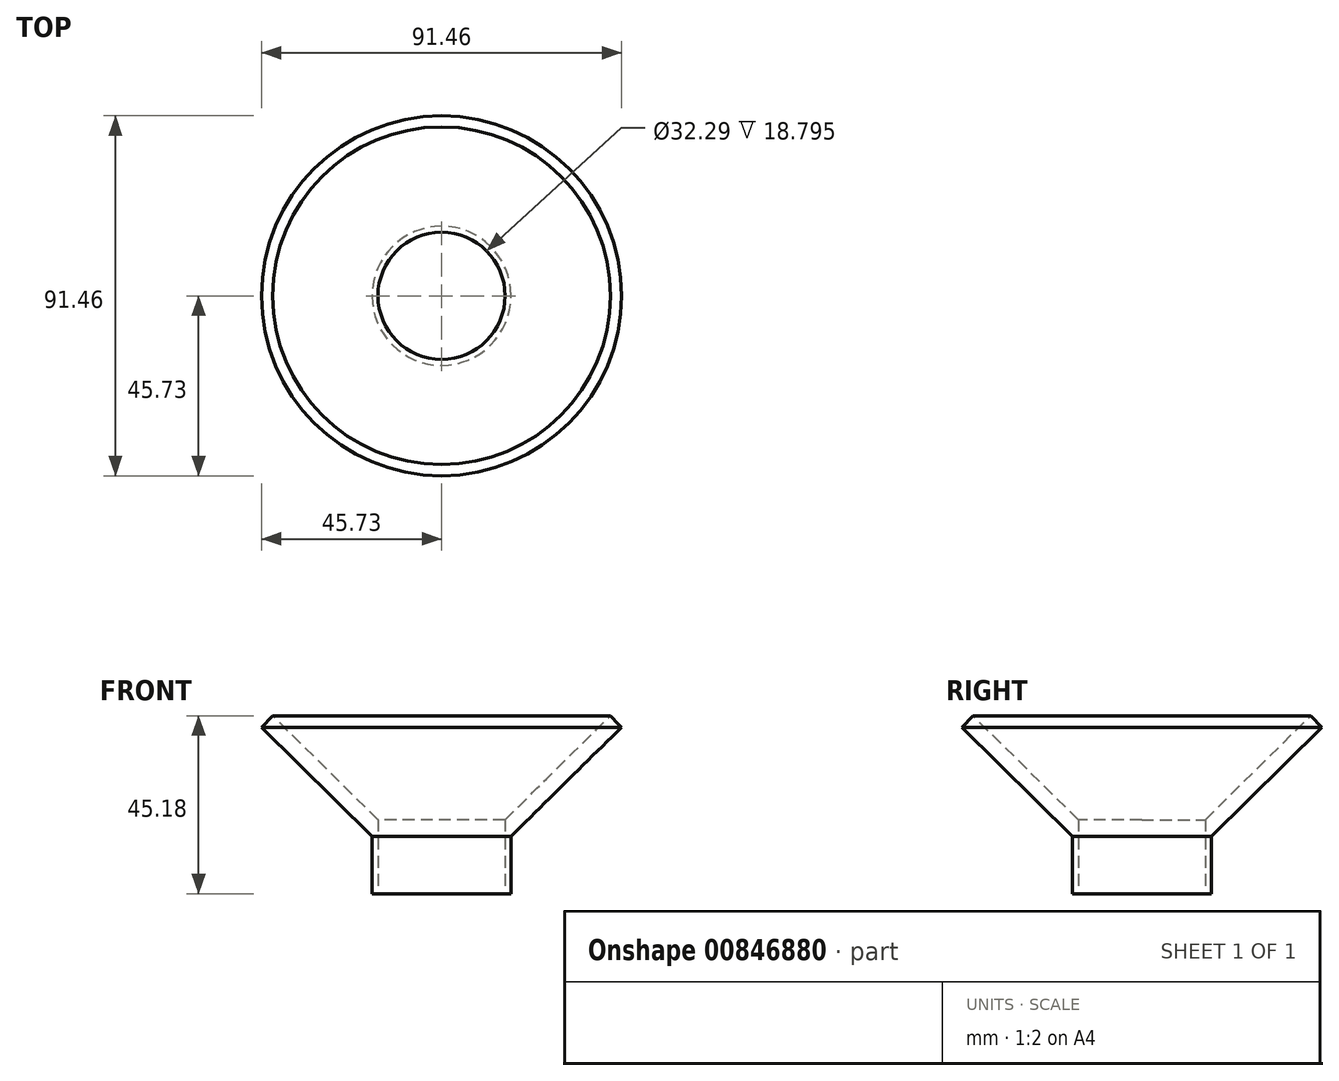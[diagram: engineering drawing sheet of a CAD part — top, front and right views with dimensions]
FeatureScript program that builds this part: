
annotation { "Feature Type Name" : "Feature", "Feature Type Description" : "" }
export const myFeature = defineFeature(function(context is Context, id is Id, definition is map)
    precondition{}
    {
        {
            var Q0;
            Q0=qCreatedBy(makeId("Front.planeOp"),FACE);
            var sketch = newSketch(context, id + "F0", { "sketchPlane" : qUnion([Q0])});
            skLineSegment(sketch, "E0", {"start": v(0, 0) * mm, "end": v(17.66, 0) * mm});
            skLineSegment(sketch, "E1", {"start": v(17.66, 0) * mm, "end": v(17.66, 14.6) * mm});
            skLineSegment(sketch, "E2", {"start": v(17.66, 14.6) * mm, "end": v(45.73, 42.3) * mm});
            skLineSegment(sketch, "E3", {"start": v(45.73, 42.3) * mm, "end": v(42.9, 45.18) * mm});
            skLineSegment(sketch, "E4", {"start": v(42.9, 45.18) * mm, "end": v(15.76, 18.42) * mm});
            skLineSegment(sketch, "E5", {"start": v(15.76, 18.42) * mm, "end": v(0, 18.42) * mm});
            skLineSegment(sketch, "E6", {"start": v(0, 18.42) * mm, "end": v(0, 0) * mm});
            skSolve(sketch);
        }
        {
            var Q0;
            Q0=makeQuery(id+"F0.imprint","IMPRINT",FACE,{"disambiguationData":[TD([[makeQuery(id+"F0.imprint","IMPRINT",EDGE,{"derivedFrom":sQuery(id+"F0.wireOp",EDGE,"E0")}),1.0]])]});
            var Q1;
            Q1=sQuery(id+"F0.wireOp",EDGE,"E6");
            revolve(context, id + "F1", {"surfaceOperationType" : NewSurfaceOperationType.NEW, "entities" : qUnion([Q0]), "axis" : qUnion([Q1]), "revolveType" : RevolveType.FULL});
        }
        {
            var Q0;
            Q0=makeQuery(id+"F1.opRevolve","SWEPT_FACE",FACE,{"disambiguationData":[OSD([sQuery(id+"F0.wireOp",EDGE,"E0")])]});
            var sketch = newSketch(context, id + "F2", { "sketchPlane" : qUnion([Q0])});
            skCircle(sketch, "E7", {"center": v(0, 0) * mm, "radius": 16.14 * mm});
            skSolve(sketch);
        }
        {
            var Q0;
            Q0=qSketchRegion(id+"F2",true);
            extrude(context, id + "F3", {"entities" : qUnion([Q0]), "operationType" : NewBodyOperationType.REMOVE, "oppositeDirection" : true, "depth" : 25.4 * mm, "offsetDistance" : 25.4 * mm});
        }
    });
